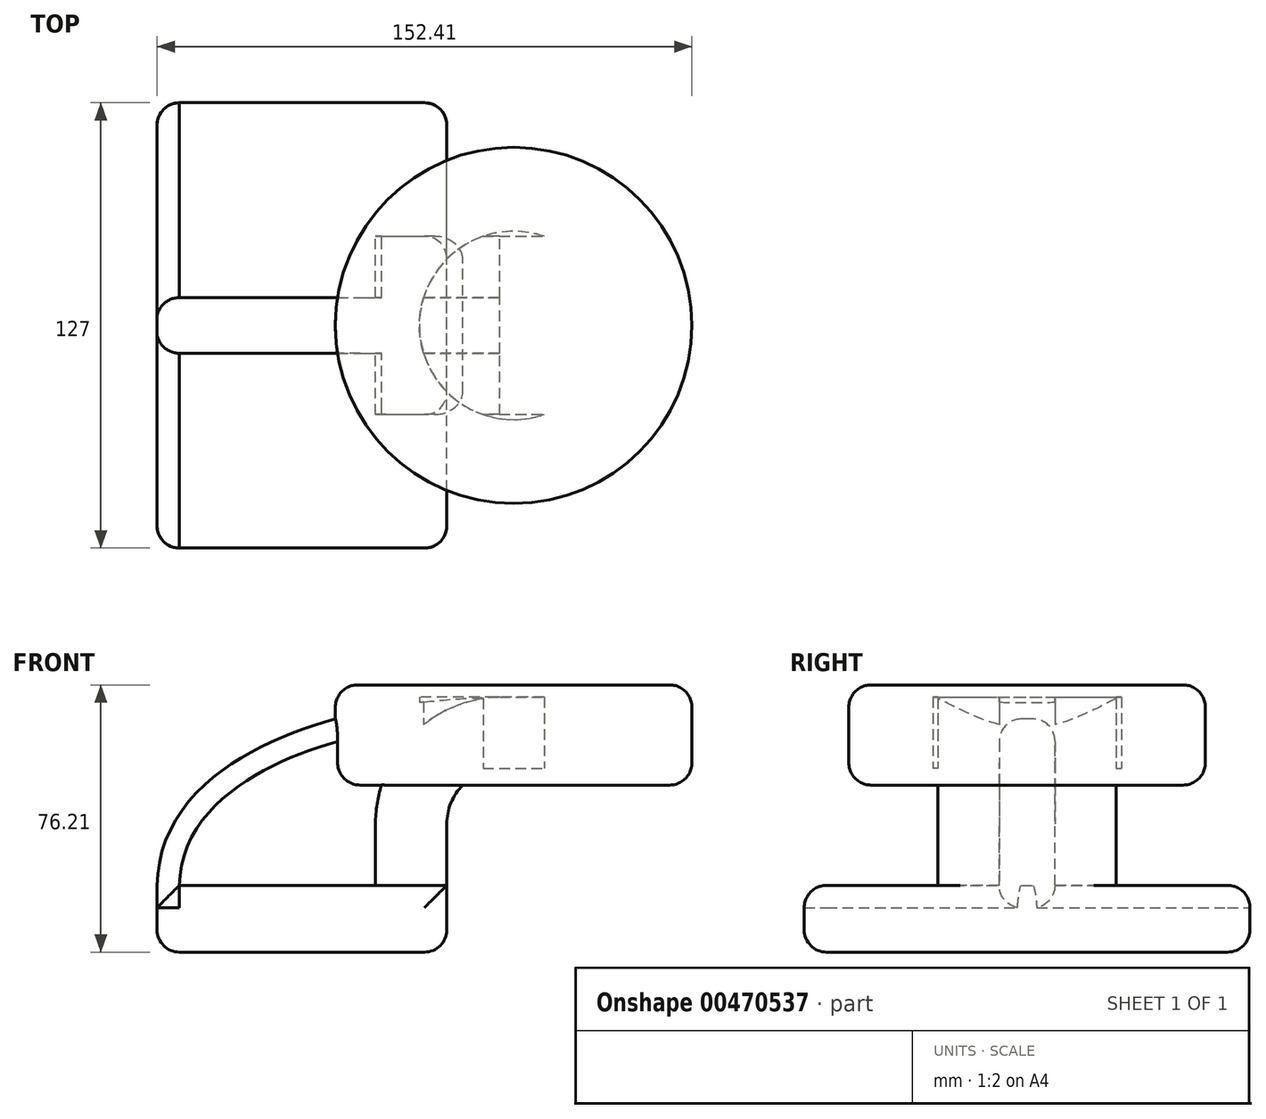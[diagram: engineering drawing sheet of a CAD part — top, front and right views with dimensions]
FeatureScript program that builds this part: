
annotation { "Feature Type Name" : "Feature", "Feature Type Description" : "" }
export const myFeature = defineFeature(function(context is Context, id is Id, definition is map)
    precondition{}
    {
        {
            var Q0;
            Q0=qCreatedBy(makeId("Front.planeOp"),FACE);
            var sketch = newSketch(context, id + "F0", { "sketchPlane" : qUnion([Q0])});
            skLineSegment(sketch, "E0.bottom", {"start": v(-41.28, 9.52) * mm, "end": v(41.28, 9.53) * mm});
            skLineSegment(sketch, "E0.top", {"start": v(-41.28, -9.53) * mm, "end": v(41.28, -9.53) * mm});
            skLineSegment(sketch, "E0.left", {"start": v(-41.28, 9.52) * mm, "end": v(-41.28, -9.53) * mm});
            skLineSegment(sketch, "E0.right", {"start": v(41.27, 9.53) * mm, "end": v(41.28, -9.52) * mm});
            skPoint(sketch, "E0.middle", {"position": v(0, 0) * mm});
            skLineSegment(sketch, "E1.bottom", {"start": v(60.32, 38.1) * mm, "end": v(111.12, 38.1) * mm});
            skLineSegment(sketch, "E1.top", {"start": v(60.32, 66.68) * mm, "end": v(111.12, 66.68) * mm});
            skLineSegment(sketch, "E1.left", {"start": v(60.32, 38.1) * mm, "end": v(60.32, 66.68) * mm});
            skLineSegment(sketch, "E1.right", {"start": v(111.12, 38.1) * mm, "end": v(111.12, 66.68) * mm});
            skPoint(sketch, "E1.middle", {"position": v(85.72, 52.39) * mm});
            skLineSegment(sketch, "E2", {"start": v(41.27, 9.53) * mm, "end": v(41.27, 27) * mm});
            skArc(sketch, "E3", {"start": v(41.27, 27) * mm, "mid": v(45.92, 38.23) * mm, "end": v(57.15, 42.88) * mm});
            skLineSegment(sketch, "E4", {"start": v(57.15, 42.88) * mm, "end": v(87.17, 42.88) * mm});
            skLineSegment(sketch, "E5.0", {"start": v(57.15, 63.2) * mm, "end": v(87.17, 63.2) * mm});
            skArc(sketch, "E5.1", {"start": v(20.95, 27) * mm, "mid": v(31.56, 52.6) * mm, "end": v(57.15, 63.2) * mm});
            skLineSegment(sketch, "E5.2", {"start": v(20.95, 9.53) * mm, "end": v(20.95, 27) * mm});
            skFitSpline(sketch, "E6", {"points": [v(-41.28, 9.53) * mm, v(57.15, 63.2) * mm], "startDerivative": vector(1.95, 110.08) * mm, "endDerivative": vector(142.9, 1.33) * mm});
            skLineSegment(sketch, "E7", {"start": v(87.17, 63.2) * mm, "end": v(87.17, 42.88) * mm});
            skSolve(sketch);
        }
        {
            var Q0;
            Q0=makeQuery(id+"F0.imprint","IMPRINT",FACE,{"disambiguationData":[TD([[makeQuery(id+"F0.imprint","IMPRINT",EDGE,{"derivedFrom":sQuery(id+"F0.wireOp",EDGE,"E0.top")}),1.0]])]});
            extrude(context, id + "F1", {"entities" : qUnion([Q0]), "endBound" : BoundingType.SYMMETRIC, "depth" : 127 * mm});
        }
        {
            var Q0;
            {var subQ1=sQuery(id+"F0.wireOp",EDGE,"E2");Q0=makeQuery(id+"F0.imprint","IMPRINT",FACE,{"disambiguationData":[TD([[makeQuery(id+"F0.imprint","IMPRINT",EDGE,{"derivedFrom":subQ1}),1.0]])]});}
            var Q1;
            {var subQ5=sQuery(id+"F0.wireOp",EDGE,"E7");Q1=makeQuery(id+"F0.imprint","IMPRINT",FACE,{"disambiguationData":[TD([[makeQuery(id+"F0.imprint","IMPRINT",EDGE,{"derivedFrom":subQ5}),-1.0]])]});}
            extrude(context, id + "F2", {"entities" : qUnion([Q0, Q1]), "operationType" : NewBodyOperationType.ADD, "endBound" : BoundingType.SYMMETRIC, "depth" : 50.8 * mm});
        }
        {
            var Q0;
            {var subQ3=sQuery(id+"F0.wireOp",EDGE,"E5.2");Q0=makeQuery(id+"F0.imprint","IMPRINT",FACE,{"disambiguationData":[TD([[makeQuery(id+"F0.imprint","IMPRINT",EDGE,{"derivedFrom":subQ3}),1.0]])]});}
            extrude(context, id + "F3", {"entities" : qUnion([Q0]), "operationType" : NewBodyOperationType.ADD, "endBound" : BoundingType.SYMMETRIC, "depth" : 15.88 * mm});
        }
        {
            var Q0;
            {var subQ4=sQuery(id+"F0.wireOp",EDGE,"E1.bottom");Q0=makeQuery(id+"F0.imprint","IMPRINT",FACE,{"disambiguationData":[TD([[makeQuery(id+"F0.imprint","IMPRINT",EDGE,{"derivedFrom":subQ4}),1.0]])]});}
            var Q1;
            Q1=sQuery(id+"F0.wireOp",EDGE,"E1.left");
            revolve(context, id + "F4", {"operationType" : NewBodyOperationType.ADD, "entities" : qUnion([Q0]), "axis" : qUnion([Q1]), "revolveType" : RevolveType.FULL});
        }
        {
            var Q0;
            Q0=makeQuery(id+"F1.opExtrude","CAP_EDGE",EDGE,{"disambiguationData":[OSD([sQuery(id+"F0.wireOp",EDGE,"E0.left")])],"isStart":false});
            var Q1;
            Q1=makeQuery(id+"F1.opExtrude","CAP_EDGE",EDGE,{"disambiguationData":[OSD([sQuery(id+"F0.wireOp",EDGE,"E0.right")])],"isStart":false});
            var Q2;
            Q2=makeQuery(id+"F1.opExtrude","CAP_EDGE",EDGE,{"disambiguationData":[OSD([sQuery(id+"F0.wireOp",EDGE,"E0.right")])],"isStart":true});
            var Q3;
            Q3=makeQuery(id+"F1.opExtrude","CAP_EDGE",EDGE,{"disambiguationData":[OSD([sQuery(id+"F0.wireOp",EDGE,"E0.left")])],"isStart":true});
            var Q4;
            Q4=makeQuery(id+"F2.opExtrude","CAP_EDGE",EDGE,{"disambiguationData":[OSD([sQuery(id+"F0.wireOp",EDGE,"E0.bottom")])],"isStart":true});
            var Q5;
            Q5=makeQuery(id+"F2.opExtrude","CAP_EDGE",EDGE,{"disambiguationData":[OSD([sQuery(id+"F0.wireOp",EDGE,"E0.bottom")])],"isStart":false});
            var Q6;
            {var subQ0=sQuery(id+"F0.wireOp",EDGE,"E0.bottom");var subQ1=sQuery(id+"F0.wireOp",EDGE,"E6");var subQ2=sQuery(id+"F0.wireOp",EDGE,"E5.2");var subQ3=sQuery(id+"F0.wireOp",EDGE,"E5.1");Q6=makeQuery(id+"F3.boolean.opBoolean","SPLIT",EDGE,{"disambiguationData":[TD([makeQuery(id+"F3.opExtrude","CAP_FACE",FACE,{"disambiguationData":[OSD([subQ0,subQ3,subQ2,subQ1])],"isStart":false})])],"derivedFrom":makeQuery(id+"F2.opExtrude","SWEPT_EDGE",EDGE,{"disambiguationData":[OSD([subQ0,subQ2])]})});}
            var Q7;
            {var subQ0=sQuery(id+"F0.wireOp",EDGE,"E6");var subQ1=sQuery(id+"F0.wireOp",EDGE,"E0.bottom");Q7=makeQuery(id+"F4.boolean.opBoolean","SPLIT",EDGE,{"disambiguationData":[TD([makeQuery(id+"F1.opExtrude","SWEPT_FACE",FACE,{"disambiguationData":[OSD([subQ1])]})])],"derivedFrom":makeQuery(id+"F3.opExtrude","CAP_EDGE",EDGE,{"disambiguationData":[OSD([subQ0])],"isStart":false})});}
            var Q8;
            {var subQ0=sQuery(id+"F0.wireOp",EDGE,"E6");var subQ1=sQuery(id+"F0.wireOp",EDGE,"E0.bottom");Q8=makeQuery(id+"F4.boolean.opBoolean","SPLIT",EDGE,{"disambiguationData":[TD([makeQuery(id+"F1.opExtrude","SWEPT_FACE",FACE,{"disambiguationData":[OSD([subQ1])]})])],"derivedFrom":makeQuery(id+"F3.opExtrude","CAP_EDGE",EDGE,{"disambiguationData":[OSD([subQ0])],"isStart":true})});}
            var Q9;
            Q9=makeQuery(id+"F4.opRevolve","SWEPT_EDGE",EDGE,{"disambiguationData":[OSD([sQuery(id+"F0.wireOp",EDGE,"E1.bottom"),sQuery(id+"F0.wireOp",EDGE,"E1.right")])]});
            var Q10;
            Q10=makeQuery(id+"F4.opRevolve","SWEPT_EDGE",EDGE,{"disambiguationData":[OSD([sQuery(id+"F0.wireOp",EDGE,"E1.top"),sQuery(id+"F0.wireOp",EDGE,"E1.right")])]});
            var Q11;
            Q11=makeQuery(id+"F1.opExtrude","CAP_EDGE",EDGE,{"disambiguationData":[OSD([sQuery(id+"F0.wireOp",EDGE,"E0.bottom")])],"isStart":false});
            var Q12;
            {var subQ0=sQuery(id+"F0.wireOp",EDGE,"E0.bottom");var subQ1=sQuery(id+"F0.wireOp",EDGE,"E6");var subQ2=sQuery(id+"F0.wireOp",EDGE,"E5.2");var subQ3=sQuery(id+"F0.wireOp",EDGE,"E5.1");Q12=makeQuery(id+"F3.boolean.opBoolean","SPLIT",EDGE,{"disambiguationData":[TD([makeQuery(id+"F3.opExtrude","CAP_FACE",FACE,{"disambiguationData":[OSD([subQ0,subQ3,subQ2,subQ1])],"isStart":true})])],"derivedFrom":makeQuery(id+"F2.opExtrude","SWEPT_EDGE",EDGE,{"disambiguationData":[OSD([subQ0,subQ2])]})});}
            var Q13;
            Q13=makeQuery(id+"F1.opExtrude","CAP_EDGE",EDGE,{"disambiguationData":[OSD([sQuery(id+"F0.wireOp",EDGE,"E0.bottom")])],"isStart":true});
            var Q14;
            Q14=makeQuery(id+"F1.opExtrude","CAP_EDGE",EDGE,{"disambiguationData":[OSD([sQuery(id+"F0.wireOp",EDGE,"E0.top")])],"isStart":true});
            var Q15;
            Q15=makeQuery(id+"F1.opExtrude","SWEPT_EDGE",EDGE,{"disambiguationData":[OSD([sQuery(id+"F0.wireOp",EDGE,"E0.top"),sQuery(id+"F0.wireOp",EDGE,"E0.left")])]});
            var Q16;
            Q16=makeQuery(id+"F1.opExtrude","CAP_EDGE",EDGE,{"disambiguationData":[OSD([sQuery(id+"F0.wireOp",EDGE,"E0.top")])],"isStart":false});
            var Q17;
            Q17=makeQuery(id+"F1.opExtrude","SWEPT_EDGE",EDGE,{"disambiguationData":[OSD([sQuery(id+"F0.wireOp",EDGE,"E0.top"),sQuery(id+"F0.wireOp",EDGE,"E0.right")])]});
            var Q18;
            Q18=makeQuery(id+"F2.opExtrude","CAP_EDGE",EDGE,{"disambiguationData":[OSD([sQuery(id+"F0.wireOp",EDGE,"E2")])],"isStart":false});
            var Q19;
            Q19=makeQuery(id+"F2.opExtrude","CAP_EDGE",EDGE,{"disambiguationData":[OSD([sQuery(id+"F0.wireOp",EDGE,"E2")])],"isStart":true});
            fillet(context, id + "F5", {"entities" : qUnion([Q0, Q1, Q2, Q3, Q4, Q5, Q6, Q7, Q8, Q9, Q10, Q11, Q12, Q13, Q14, Q15, Q16, Q17, Q18, Q19]), "radius" : 6.35 * mm, "tangentPropagation" : true, "allowEdgeOverflow" : false});
        }
        {
            var Q0;
            {var subQ0=sQuery(id+"F0.wireOp",EDGE,"E0.left");var subQ1=sQuery(id+"F0.wireOp",EDGE,"E0.bottom");var subQ2=sQuery(id+"F0.wireOp",EDGE,"E6");var subQ3=makeQuery(id+"F1.opExtrude","SWEPT_EDGE",EDGE,{"disambiguationData":[OSD([subQ1,subQ0,subQ2])]});Q0=makeQuery(id+"F5.opFillet","MERGE",EDGE,{"derivedFrom":[makeQuery(id+"F3.boolean.opBoolean","MERGE",EDGE,{"derivedFrom":[subQ3,makeQuery(id+"F3.opExtrude","SWEPT_EDGE",EDGE,{"disambiguationData":[OSD([subQ1,subQ0,subQ2])]})]}),makeQuery(id+"F3.boolean.opBoolean","SPLIT",EDGE,{"disambiguationData":[TD([makeQuery(id+"F1.opExtrude","CAP_FACE",FACE,{"disambiguationData":[OSD([subQ1,sQuery(id+"F0.wireOp",EDGE,"E0.top"),subQ0,sQuery(id+"F0.wireOp",EDGE,"E0.right")])],"isStart":false})])],"derivedFrom":subQ3})]});}
            var Q1;
            {var subQ0=sQuery(id+"F0.wireOp",EDGE,"E0.left");var subQ1=sQuery(id+"F0.wireOp",EDGE,"E0.bottom");var subQ2=sQuery(id+"F0.wireOp",EDGE,"E6");var subQ3=makeQuery(id+"F1.opExtrude","SWEPT_EDGE",EDGE,{"disambiguationData":[OSD([subQ1,subQ0,subQ2])]});Q1=makeQuery(id+"F5.opFillet","MERGE",EDGE,{"derivedFrom":[makeQuery(id+"F3.boolean.opBoolean","MERGE",EDGE,{"derivedFrom":[subQ3,makeQuery(id+"F3.opExtrude","SWEPT_EDGE",EDGE,{"disambiguationData":[OSD([subQ1,subQ0,subQ2])]})]}),makeQuery(id+"F3.boolean.opBoolean","SPLIT",EDGE,{"disambiguationData":[TD([makeQuery(id+"F1.opExtrude","CAP_FACE",FACE,{"disambiguationData":[OSD([subQ1,sQuery(id+"F0.wireOp",EDGE,"E0.top"),subQ0,sQuery(id+"F0.wireOp",EDGE,"E0.right")])],"isStart":true})])],"derivedFrom":subQ3})]});}
            chamfer(context, id + "F6", {"entities" : qUnion([Q0, Q1]), "width" : 6.35 * mm, "tangentPropagation" : true});
        }
    });
